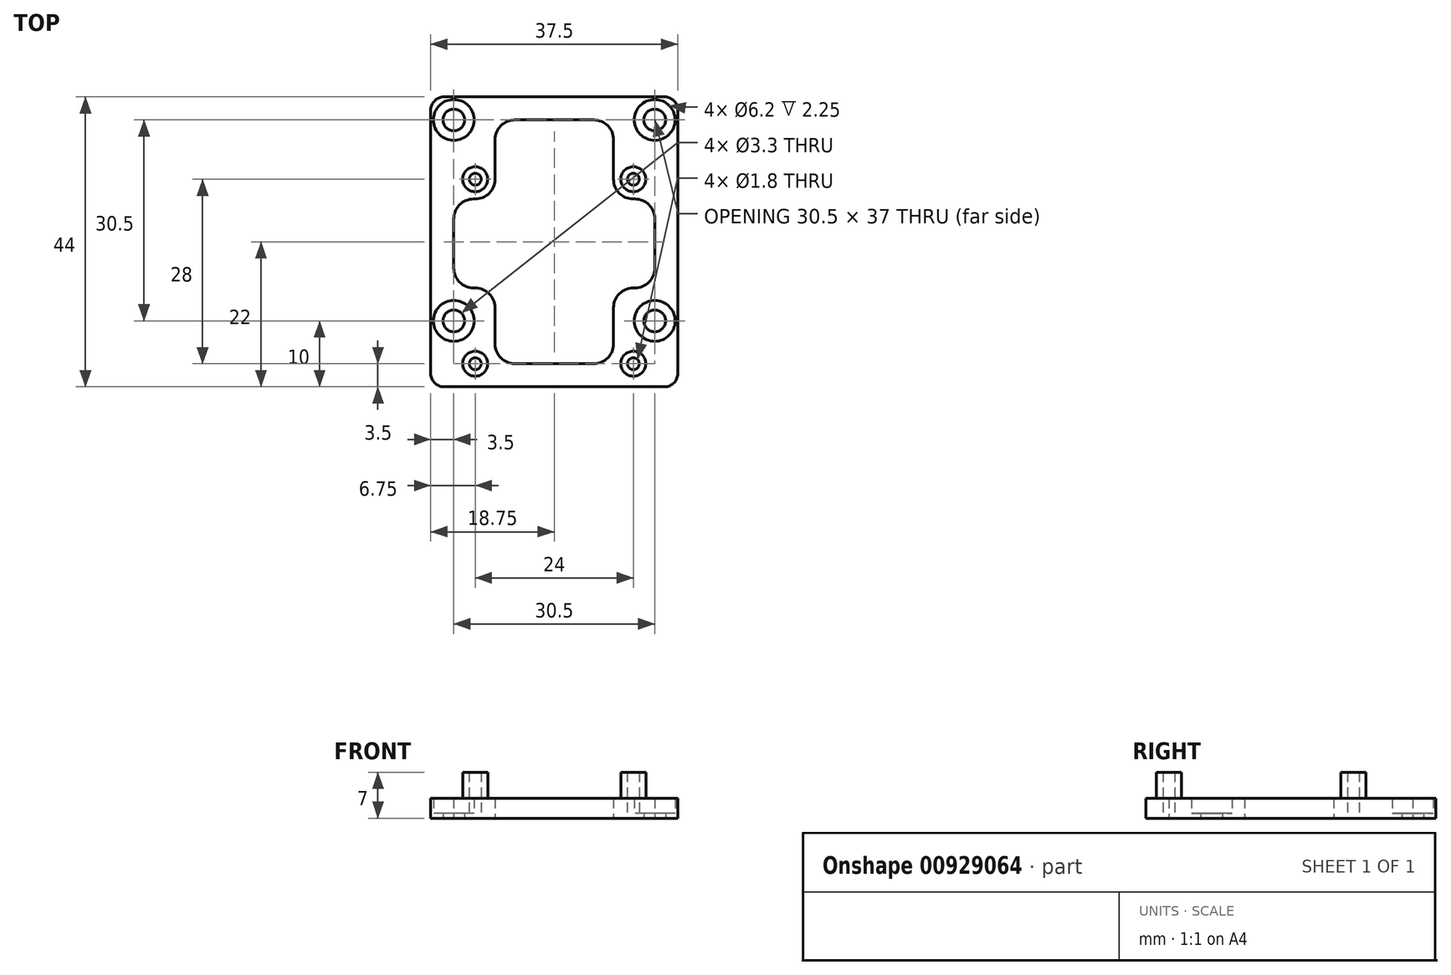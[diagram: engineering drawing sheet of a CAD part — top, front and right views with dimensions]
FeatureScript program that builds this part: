
annotation { "Feature Type Name" : "Feature", "Feature Type Description" : "" }
export const myFeature = defineFeature(function(context is Context, id is Id, definition is map)
    precondition{}
    {
        {
            var Q0;
            Q0=qCreatedBy(makeId("Top.planeOp"),FACE);
            var sketch = newSketch(context, id + "F0", { "sketchPlane" : qUnion([Q0])});
            skPoint(sketch, "E0.middle", {"position": v(0, 0) * mm});
            skCircle(sketch, "E1", {"center": v(-12, 14) * mm, "radius": 0.9 * mm});
            skLineSegment(sketch, "E2", {"start": v(-12, 14) * mm, "end": v(9, 14) * mm, "construction": true});
            skCircle(sketch, "E3", {"center": v(12, 14) * mm, "radius": 0.9 * mm});
            skLineSegment(sketch, "E4", {"start": v(12, 14) * mm, "end": v(12, -14) * mm, "construction": true});
            skCircle(sketch, "E5", {"center": v(12, -14) * mm, "radius": 0.9 * mm});
            skLineSegment(sketch, "E6", {"start": v(12, -14) * mm, "end": v(-12, -14) * mm, "construction": true});
            skCircle(sketch, "E7", {"center": v(-12, -14) * mm, "radius": 0.9 * mm});
            skLineSegment(sketch, "E8", {"start": v(12, 0) * mm, "end": v(-12, 0) * mm, "construction": true});
            skLineSegment(sketch, "E9.0", {"start": v(-18.75, 24.5) * mm, "end": v(-18.75, -15.5) * mm});
            skLineSegment(sketch, "E9.1", {"start": v(-16.75, 26.5) * mm, "end": v(16.75, 26.5) * mm});
            skLineSegment(sketch, "E9.2", {"start": v(18.75, 24.5) * mm, "end": v(18.75, -15.5) * mm});
            skLineSegment(sketch, "E9.3", {"start": v(-16.75, -17.5) * mm, "end": v(16.75, -17.5) * mm});
            skPoint(sketch, "E10.visualSharp", {"position": v(-18.75, 26.5) * mm});
            skArc(sketch, "E10.filletArc", {"start": v(-16.75, 26.5) * mm, "mid": v(-18.16, 25.91) * mm, "end": v(-18.75, 24.5) * mm});
            skPoint(sketch, "E11.visualSharp", {"position": v(18.75, 26.5) * mm});
            skArc(sketch, "E11.filletArc", {"start": v(18.75, 24.5) * mm, "mid": v(18.16, 25.91) * mm, "end": v(16.75, 26.5) * mm});
            skPoint(sketch, "E12.visualSharp", {"position": v(18.75, -17.5) * mm});
            skArc(sketch, "E12.filletArc", {"start": v(16.75, -17.5) * mm, "mid": v(18.16, -16.91) * mm, "end": v(18.75, -15.5) * mm});
            skPoint(sketch, "E13.visualSharp", {"position": v(-18.75, -17.5) * mm});
            skArc(sketch, "E13.filletArc", {"start": v(-18.75, -15.5) * mm, "mid": v(-18.16, -16.91) * mm, "end": v(-16.75, -17.5) * mm});
            skLineSegment(sketch, "E14", {"start": v(-15.25, 23) * mm, "end": v(15.25, 23) * mm, "construction": true});
            skCircle(sketch, "E15", {"center": v(-15.25, 23) * mm, "radius": 1.65 * mm});
            skCircle(sketch, "E16", {"center": v(15.25, 23) * mm, "radius": 1.65 * mm});
            skLineSegment(sketch, "E17", {"start": v(0, 0) * mm, "end": v(0, 23) * mm, "construction": true});
            skLineSegment(sketch, "E18", {"start": v(-15.25, 23) * mm, "end": v(-15.25, -7.5) * mm, "construction": true});
            skCircle(sketch, "E19", {"center": v(-15.25, -7.5) * mm, "radius": 1.65 * mm});
            skLineSegment(sketch, "E20", {"start": v(-15.25, -7.5) * mm, "end": v(15.25, -7.5) * mm, "construction": true});
            skCircle(sketch, "E21", {"center": v(15.25, -7.5) * mm, "radius": 1.65 * mm});
            skLineSegment(sketch, "E22", {"start": v(15.25, -7.5) * mm, "end": v(15.25, 23) * mm, "construction": true});
            skCircle(sketch, "E23.0", {"center": v(-15.25, 23) * mm, "radius": 3.1 * mm});
            skCircle(sketch, "E24.MirrorC", {"center": v(15.25, 23) * mm, "radius": 3.1 * mm});
            skLineSegment(sketch, "E25", {"start": v(-15.25, 7.75) * mm, "end": v(-6.92, 7.75) * mm, "construction": true});
            skCircle(sketch, "E26.MirrorC", {"center": v(-15.25, -7.5) * mm, "radius": 3.1 * mm});
            skCircle(sketch, "E27.MirrorC", {"center": v(15.25, -7.5) * mm, "radius": 3.1 * mm});
            skLineSegment(sketch, "E28", {"start": v(-9.75, -14) * mm, "end": v(-9.75, -7.5) * mm});
            skLineSegment(sketch, "E29", {"start": v(-9.75, 14) * mm, "end": v(9.75, 14) * mm});
            skLineSegment(sketch, "E30", {"start": v(9.75, -14) * mm, "end": v(-9.75, -14) * mm});
            skCircle(sketch, "E31.0", {"center": v(-12, 14) * mm, "radius": 1.9 * mm});
            skCircle(sketch, "E32.0", {"center": v(12, -14) * mm, "radius": 1.9 * mm});
            skCircle(sketch, "E33.0", {"center": v(-12, -14) * mm, "radius": 1.9 * mm});
            skCircle(sketch, "E34.0", {"center": v(12, 14) * mm, "radius": 1.9 * mm});
            skLineSegment(sketch, "E35", {"start": v(-9, 11) * mm, "end": v(-9, 23) * mm});
            skLineSegment(sketch, "E36", {"start": v(-9, 23) * mm, "end": v(9, 23) * mm});
            skLineSegment(sketch, "E37", {"start": v(9, 23) * mm, "end": v(9, 14) * mm});
            skLineSegment(sketch, "E38", {"start": v(-9, 11) * mm, "end": v(-15.25, 11) * mm});
            skLineSegment(sketch, "E39", {"start": v(-15.25, 11) * mm, "end": v(-15.25, -2.5) * mm});
            skLineSegment(sketch, "E40", {"start": v(-15.25, -2.5) * mm, "end": v(-9.75, -2.5) * mm});
            skPoint(sketch, "E41.orphan", {"position": v(-9, 14) * mm});
            skLineSegment(sketch, "E42", {"start": v(15.25, 11) * mm, "end": v(9, 11) * mm});
            skLineSegment(sketch, "E43", {"start": v(9, 11) * mm, "end": v(9, 14) * mm});
            skLineSegment(sketch, "E44.trimOffspring", {"start": v(9.75, 14) * mm, "end": v(12, 14) * mm, "construction": true});
            skLineSegment(sketch, "E45", {"start": v(15.25, -2.5) * mm, "end": v(9.75, -2.5) * mm});
            skLineSegment(sketch, "E46", {"start": v(9.75, -2.5) * mm, "end": v(9, -2.5) * mm});
            skLineSegment(sketch, "E47", {"start": v(9, -2.5) * mm, "end": v(9, -14) * mm});
            skLineSegment(sketch, "E48.trimOffspring", {"start": v(9.75, -7.5) * mm, "end": v(9.75, -14) * mm});
            skLineSegment(sketch, "E49", {"start": v(-9.75, -2.5) * mm, "end": v(-9, -2.5) * mm});
            skLineSegment(sketch, "E50", {"start": v(-9, -2.5) * mm, "end": v(-9, -14) * mm});
            skLineSegment(sketch, "E51", {"start": v(-9, -14) * mm, "end": v(9, -14) * mm});
            skLineSegment(sketch, "E52", {"start": v(15.25, 11) * mm, "end": v(15.25, -2.5) * mm});
            skSolve(sketch);
        }
        {
            var Q0;
            Q0=makeQuery(id+"F0.imprint","IMPRINT",FACE,{"disambiguationData":[TD([[makeQuery(id+"F0.imprint","IMPRINT",EDGE,{"derivedFrom":sQuery(id+"F0.wireOp",EDGE,"E9.0")}),1.0]])]});
            extrude(context, id + "F1", {"entities" : qUnion([Q0]), "depth" : 3 * mm, "offsetDistance" : 25 * mm});
        }
        {
            var Q0;
            Q0=makeQuery(id+"F0.imprint","IMPRINT",FACE,{"disambiguationData":[TD([[makeQuery(id+"F0.imprint","IMPRINT",EDGE,{"derivedFrom":sQuery(id+"F0.wireOp",EDGE,"E15")}),-1.0]])]});
            var Q1;
            Q1=makeQuery(id+"F0.imprint","IMPRINT",FACE,{"disambiguationData":[TD([[makeQuery(id+"F0.imprint","IMPRINT",EDGE,{"derivedFrom":sQuery(id+"F0.wireOp",EDGE,"E16")}),-1.0]])]});
            var Q2;
            Q2=makeQuery(id+"F0.imprint","IMPRINT",FACE,{"disambiguationData":[TD([[makeQuery(id+"F0.imprint","IMPRINT",EDGE,{"derivedFrom":sQuery(id+"F0.wireOp",EDGE,"E21")}),-1.0]])]});
            var Q3;
            Q3=makeQuery(id+"F0.imprint","IMPRINT",FACE,{"disambiguationData":[TD([[makeQuery(id+"F0.imprint","IMPRINT",EDGE,{"derivedFrom":sQuery(id+"F0.wireOp",EDGE,"E19")}),-1.0]])]});
            extrude(context, id + "F2", {"entities" : qUnion([Q0, Q1, Q2, Q3]), "operationType" : NewBodyOperationType.ADD, "depth" : 0.75 * mm, "offsetDistance" : 25 * mm});
        }
        {
            var Q0;
            Q0=makeQuery(id+"F0.imprint","IMPRINT",FACE,{"disambiguationData":[TD([[makeQuery(id+"F0.imprint","IMPRINT",EDGE,{"derivedFrom":sQuery(id+"F0.wireOp",EDGE,"E1")}),-1.0]])]});
            var Q1;
            Q1=makeQuery(id+"F0.imprint","IMPRINT",FACE,{"disambiguationData":[TD([[makeQuery(id+"F0.imprint","IMPRINT",EDGE,{"derivedFrom":sQuery(id+"F0.wireOp",EDGE,"E3")}),-1.0]])]});
            var Q2;
            Q2=makeQuery(id+"F0.imprint","IMPRINT",FACE,{"disambiguationData":[TD([[makeQuery(id+"F0.imprint","IMPRINT",EDGE,{"derivedFrom":sQuery(id+"F0.wireOp",EDGE,"E5")}),-1.0]])]});
            var Q3;
            Q3=makeQuery(id+"F0.imprint","IMPRINT",FACE,{"disambiguationData":[TD([[makeQuery(id+"F0.imprint","IMPRINT",EDGE,{"derivedFrom":sQuery(id+"F0.wireOp",EDGE,"E7")}),-1.0]])]});
            extrude(context, id + "F3", {"entities" : qUnion([Q0, Q1, Q2, Q3]), "operationType" : NewBodyOperationType.ADD, "depth" : 7 * mm, "offsetDistance" : 25 * mm});
        }
        {
            var Q0;
            Q0=makeQuery(id+"F1.opExtrude","SWEPT_EDGE",EDGE,{"disambiguationData":[OSD([sQuery(id+"F0.wireOp",EDGE,"E38"),sQuery(id+"F0.wireOp",EDGE,"E39")])]});
            var Q1;
            Q1=makeQuery(id+"F1.opExtrude","SWEPT_EDGE",EDGE,{"disambiguationData":[OSD([sQuery(id+"F0.wireOp",EDGE,"E35"),sQuery(id+"F0.wireOp",EDGE,"E36")])]});
            var Q2;
            Q2=makeQuery(id+"F1.opExtrude","SWEPT_EDGE",EDGE,{"disambiguationData":[OSD([sQuery(id+"F0.wireOp",EDGE,"E35"),sQuery(id+"F0.wireOp",EDGE,"E38")])]});
            var Q3;
            Q3=makeQuery(id+"F1.opExtrude","SWEPT_EDGE",EDGE,{"disambiguationData":[OSD([sQuery(id+"F0.wireOp",EDGE,"E36"),sQuery(id+"F0.wireOp",EDGE,"E37")])]});
            var Q4;
            Q4=makeQuery(id+"F1.opExtrude","SWEPT_EDGE",EDGE,{"disambiguationData":[OSD([sQuery(id+"F0.wireOp",EDGE,"E42"),sQuery(id+"F0.wireOp",EDGE,"E43")])]});
            var Q5;
            Q5=makeQuery(id+"F1.opExtrude","SWEPT_EDGE",EDGE,{"disambiguationData":[OSD([sQuery(id+"F0.wireOp",EDGE,"E42"),sQuery(id+"F0.wireOp",EDGE,"E52")])]});
            var Q6;
            Q6=makeQuery(id+"F1.opExtrude","SWEPT_EDGE",EDGE,{"disambiguationData":[OSD([sQuery(id+"F0.wireOp",EDGE,"E45"),sQuery(id+"F0.wireOp",EDGE,"E52")])]});
            var Q7;
            Q7=makeQuery(id+"F1.opExtrude","SWEPT_EDGE",EDGE,{"disambiguationData":[OSD([sQuery(id+"F0.wireOp",EDGE,"E46"),sQuery(id+"F0.wireOp",EDGE,"E47")])]});
            var Q8;
            Q8=makeQuery(id+"F1.opExtrude","SWEPT_EDGE",EDGE,{"disambiguationData":[OSD([sQuery(id+"F0.wireOp",EDGE,"E30"),sQuery(id+"F0.wireOp",EDGE,"E47")])]});
            var Q9;
            Q9=makeQuery(id+"F1.opExtrude","SWEPT_EDGE",EDGE,{"disambiguationData":[OSD([sQuery(id+"F0.wireOp",EDGE,"E49"),sQuery(id+"F0.wireOp",EDGE,"E50")])]});
            var Q10;
            Q10=makeQuery(id+"F1.opExtrude","SWEPT_EDGE",EDGE,{"disambiguationData":[OSD([sQuery(id+"F0.wireOp",EDGE,"E30"),sQuery(id+"F0.wireOp",EDGE,"E50")])]});
            var Q11;
            Q11=makeQuery(id+"F1.opExtrude","SWEPT_EDGE",EDGE,{"disambiguationData":[OSD([sQuery(id+"F0.wireOp",EDGE,"E39"),sQuery(id+"F0.wireOp",EDGE,"E40")])]});
            fillet(context, id + "F4", {"entities" : qUnion([Q0, Q1, Q2, Q3, Q4, Q5, Q6, Q7, Q8, Q9, Q10, Q11]), "radius" : 3 * mm, "tangentPropagation" : true, "allowEdgeOverflow" : false});
        }
    });
